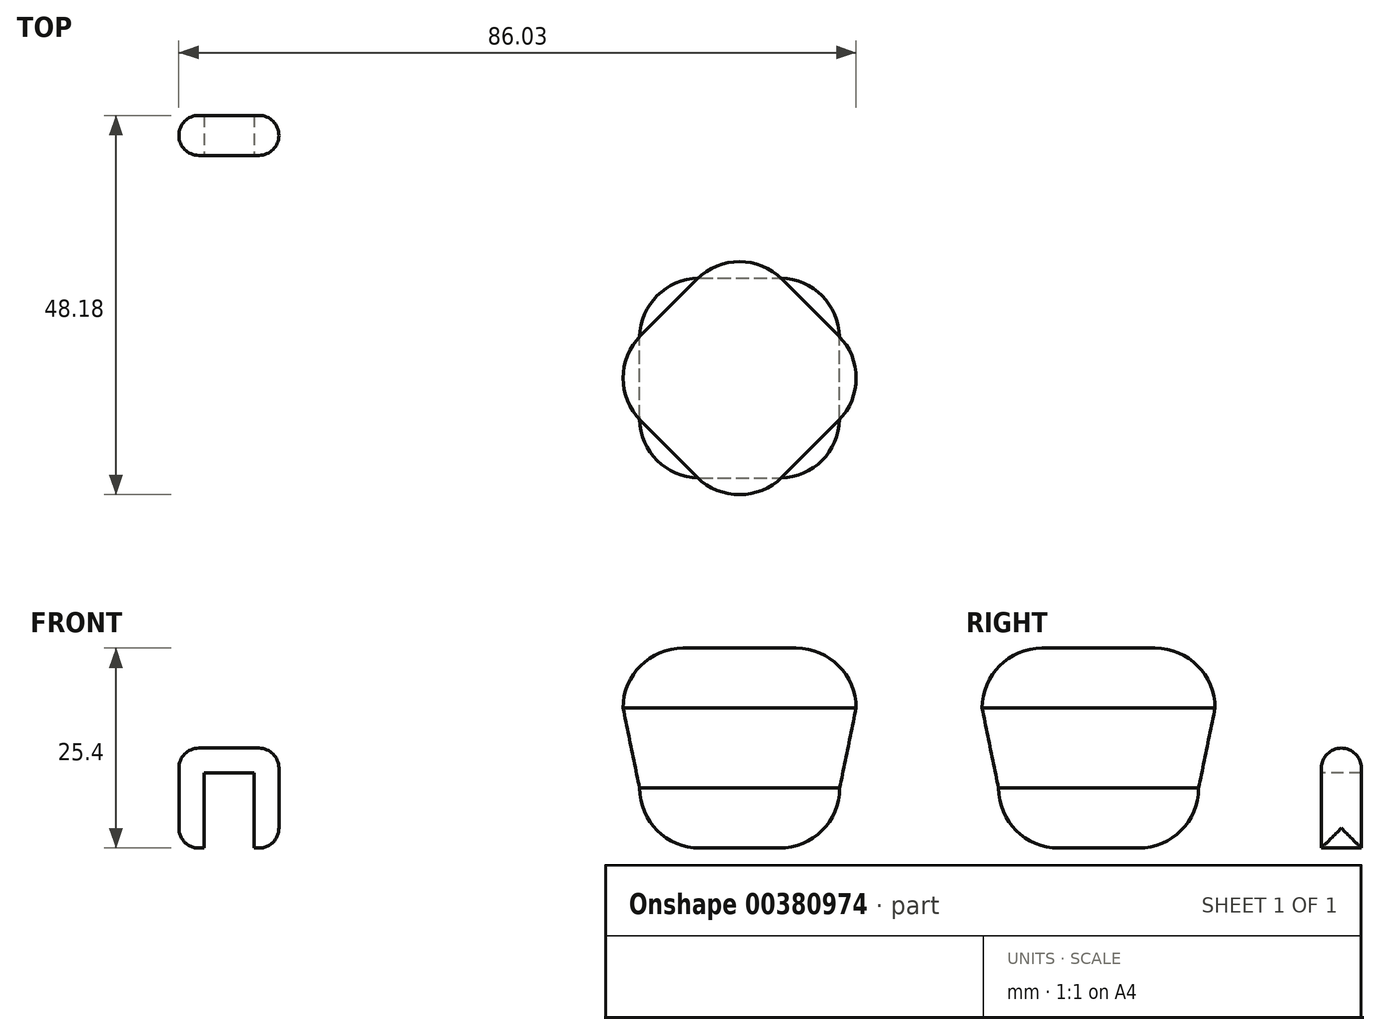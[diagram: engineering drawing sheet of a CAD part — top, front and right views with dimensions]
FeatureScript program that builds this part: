
annotation { "Feature Type Name" : "Feature", "Feature Type Description" : "" }
export const myFeature = defineFeature(function(context is Context, id is Id, definition is map)
    precondition{}
    {
        {
            var Q0;
            Q0=qCreatedBy(makeId("Top.planeOp"),FACE);
            var sketch = newSketch(context, id + "F0", { "sketchPlane" : qUnion([Q0])});
            skLineSegment(sketch, "E0.bottom", {"start": v(0, 0) * mm, "end": v(25.4, 0) * mm});
            skLineSegment(sketch, "E0.top", {"start": v(0, 25.4) * mm, "end": v(25.4, 25.4) * mm});
            skLineSegment(sketch, "E0.left", {"start": v(0, 0) * mm, "end": v(0, 25.4) * mm});
            skLineSegment(sketch, "E0.right", {"start": v(25.4, 0) * mm, "end": v(25.4, 25.4) * mm});
            skSolve(sketch);
        }
        {
            var Q0;
            Q0=makeQuery(id+"F0.imprint","IMPRINT",FACE,{"disambiguationData":[TD([[makeQuery(id+"F0.imprint","IMPRINT",EDGE,{"derivedFrom":sQuery(id+"F0.wireOp",EDGE,"E0.bottom")}),1.0]])]});
            extrude(context, id + "F1", {"entities" : qUnion([Q0]), "depth" : 7.62 * mm});
        }
        {
            var Q0;
            Q0=makeQuery(id+"F1.opExtrude","CAP_FACE",FACE,{"disambiguationData":[OSD([sQuery(id+"F0.wireOp",EDGE,"E0.bottom"),sQuery(id+"F0.wireOp",EDGE,"E0.top"),sQuery(id+"F0.wireOp",EDGE,"E0.left"),sQuery(id+"F0.wireOp",EDGE,"E0.right")])],"isStart":true});
            fillet(context, id + "F2", {"entities" : qUnion([Q0]), "radius" : 7.62 * mm, "tangentPropagation" : true, "allowEdgeOverflow" : false});
        }
        {
            var Q0;
            Q0=makeQuery(id+"F2.opFillet","BLEND_EDGE",EDGE,{"blendedFrom":[makeQuery(id+"F1.opExtrude","CAP_EDGE",EDGE,{"disambiguationData":[OSD([sQuery(id+"F0.wireOp",EDGE,"E0.bottom")])],"isStart":true}),makeQuery(id+"F1.opExtrude","CAP_EDGE",EDGE,{"disambiguationData":[OSD([sQuery(id+"F0.wireOp",EDGE,"E0.right")])],"isStart":true})],"blendedInto":[]});
            var Q1;
            Q1=makeQuery(id+"F2.opFillet","BLEND_EDGE",EDGE,{"blendedFrom":[makeQuery(id+"F1.opExtrude","CAP_EDGE",EDGE,{"disambiguationData":[OSD([sQuery(id+"F0.wireOp",EDGE,"E0.bottom")])],"isStart":true}),makeQuery(id+"F1.opExtrude","CAP_EDGE",EDGE,{"disambiguationData":[OSD([sQuery(id+"F0.wireOp",EDGE,"E0.left")])],"isStart":true})],"blendedInto":[]});
            var Q2;
            Q2=makeQuery(id+"F2.opFillet","BLEND_EDGE",EDGE,{"blendedFrom":[makeQuery(id+"F1.opExtrude","CAP_EDGE",EDGE,{"disambiguationData":[OSD([sQuery(id+"F0.wireOp",EDGE,"E0.top")])],"isStart":true}),makeQuery(id+"F1.opExtrude","CAP_EDGE",EDGE,{"disambiguationData":[OSD([sQuery(id+"F0.wireOp",EDGE,"E0.left")])],"isStart":true})],"blendedInto":[]});
            var Q3;
            Q3=makeQuery(id+"F2.opFillet","BLEND_EDGE",EDGE,{"blendedFrom":[makeQuery(id+"F1.opExtrude","CAP_EDGE",EDGE,{"disambiguationData":[OSD([sQuery(id+"F0.wireOp",EDGE,"E0.top")])],"isStart":true}),makeQuery(id+"F1.opExtrude","CAP_EDGE",EDGE,{"disambiguationData":[OSD([sQuery(id+"F0.wireOp",EDGE,"E0.right")])],"isStart":true})],"blendedInto":[]});
            fillet(context, id + "F3", {"entities" : qUnion([Q0, Q1, Q2, Q3]), "radius" : 7.62 * mm, "tangentPropagation" : true, "allowEdgeOverflow" : false});
        }
        {
            var Q0;
            Q0=makeQuery(id+"F1.opExtrude","CAP_FACE",FACE,{"disambiguationData":[OSD([sQuery(id+"F0.wireOp",EDGE,"E0.bottom"),sQuery(id+"F0.wireOp",EDGE,"E0.top"),sQuery(id+"F0.wireOp",EDGE,"E0.left"),sQuery(id+"F0.wireOp",EDGE,"E0.right")])],"isStart":false});
            cPlane(context, id + "F4", {"entities" : qUnion([Q0]), "cplaneType" : CPlaneType.OFFSET, "offset" : 10.16 * mm, "width" : 152.4 * mm, "height" : 152.4 * mm});
        }
        {
            var Q0;
            Q0=qCreatedBy(id+"F4.planeOp",FACE);
            var sketch = newSketch(context, id + "F5", { "sketchPlane" : qUnion([Q0])});
            skLineSegment(sketch, "E1", {"start": v(0, 0) * mm, "end": v(0, 25.4) * mm});
            skLineSegment(sketch, "E2", {"start": v(0, 25.4) * mm, "end": v(25.4, 25.4) * mm});
            skLineSegment(sketch, "E3", {"start": v(25.4, 25.4) * mm, "end": v(25.4, 0) * mm});
            skLineSegment(sketch, "E4", {"start": v(25.4, 0) * mm, "end": v(0, 0) * mm});
            skSolve(sketch);
        }
        {
            var Q0;
            Q0=makeQuery(id+"F5.imprint","IMPRINT",FACE,{"disambiguationData":[TD([[makeQuery(id+"F5.imprint","IMPRINT",EDGE,{"derivedFrom":sQuery(id+"F5.wireOp",EDGE,"E1")}),-1.0]])]});
            extrude(context, id + "F6", {"entities" : qUnion([Q0]), "depth" : 7.62 * mm});
        }
        {
            var Q0;
            Q0=makeQuery(id+"F6.opExtrude","CAP_FACE",FACE,{"disambiguationData":[OSD([sQuery(id+"F5.wireOp",EDGE,"E1"),sQuery(id+"F5.wireOp",EDGE,"E2"),sQuery(id+"F5.wireOp",EDGE,"E3"),sQuery(id+"F5.wireOp",EDGE,"E4")])],"isStart":false});
            fillet(context, id + "F7", {"entities" : qUnion([Q0]), "radius" : 7.62 * mm, "tangentPropagation" : true, "allowEdgeOverflow" : false});
        }
        {
            var Q0;
            Q0=makeQuery(id+"F7.opFillet","BLEND_EDGE",EDGE,{"blendedFrom":[makeQuery(id+"F6.opExtrude","CAP_EDGE",EDGE,{"disambiguationData":[OSD([sQuery(id+"F5.wireOp",EDGE,"E3")])],"isStart":false}),makeQuery(id+"F6.opExtrude","CAP_EDGE",EDGE,{"disambiguationData":[OSD([sQuery(id+"F5.wireOp",EDGE,"E4")])],"isStart":false})],"blendedInto":[]});
            var Q1;
            Q1=makeQuery(id+"F7.opFillet","BLEND_EDGE",EDGE,{"blendedFrom":[makeQuery(id+"F6.opExtrude","CAP_EDGE",EDGE,{"disambiguationData":[OSD([sQuery(id+"F5.wireOp",EDGE,"E1")])],"isStart":false}),makeQuery(id+"F6.opExtrude","CAP_EDGE",EDGE,{"disambiguationData":[OSD([sQuery(id+"F5.wireOp",EDGE,"E4")])],"isStart":false})],"blendedInto":[]});
            var Q2;
            Q2=makeQuery(id+"F7.opFillet","BLEND_EDGE",EDGE,{"blendedFrom":[makeQuery(id+"F6.opExtrude","CAP_EDGE",EDGE,{"disambiguationData":[OSD([sQuery(id+"F5.wireOp",EDGE,"E1")])],"isStart":false}),makeQuery(id+"F6.opExtrude","CAP_EDGE",EDGE,{"disambiguationData":[OSD([sQuery(id+"F5.wireOp",EDGE,"E2")])],"isStart":false})],"blendedInto":[]});
            var Q3;
            Q3=makeQuery(id+"F7.opFillet","BLEND_EDGE",EDGE,{"blendedFrom":[makeQuery(id+"F6.opExtrude","CAP_EDGE",EDGE,{"disambiguationData":[OSD([sQuery(id+"F5.wireOp",EDGE,"E2")])],"isStart":false}),makeQuery(id+"F6.opExtrude","CAP_EDGE",EDGE,{"disambiguationData":[OSD([sQuery(id+"F5.wireOp",EDGE,"E3")])],"isStart":false})],"blendedInto":[]});
            fillet(context, id + "F8", {"entities" : qUnion([Q0, Q1, Q2, Q3]), "radius" : 7.62 * mm, "tangentPropagation" : true, "allowEdgeOverflow" : false});
        }
        {
            var Q0;
            Q0=qCreatedBy(makeId("Front.planeOp"),FACE);
            cPlane(context, id + "F9", {"entities" : qUnion([Q0]), "cplaneType" : CPlaneType.OFFSET, "offset" : 12.7 * mm, "oppositeDirection" : true, "width" : 152.4 * mm, "height" : 152.4 * mm});
        }
        {
            var Q0;
            Q0=qCreatedBy(id+"F9.planeOp",FACE);
            var sketch = newSketch(context, id + "F10", { "sketchPlane" : qUnion([Q0])});
            skLineSegment(sketch, "E5.0", {"start": v(17.78, 25.4) * mm, "end": v(7.62, 25.4) * mm});
            skLineSegment(sketch, "E6", {"start": v(12.7, 25.4) * mm, "end": v(12.7, 70.24) * mm, "construction": true});
            skSolve(sketch);
        }
        {
            var Q0;
            Q0=makeQuery(id+"F6.opExtrude","SWEPT_BODY",BODY,{"disambiguationData":[OSD([sQuery(id+"F5.wireOp",EDGE,"E1"),sQuery(id+"F5.wireOp",EDGE,"E2"),sQuery(id+"F5.wireOp",EDGE,"E3"),sQuery(id+"F5.wireOp",EDGE,"E4")])]});
            var Q1;
            Q1=sQuery(id+"F10.wireOp",EDGE,"E6");
            transform(context, id + "F11", {"entities" : qUnion([Q0]), "transformType" : TransformType.ROTATION, "transformAxis" : qUnion([Q1]), "angle" : 45 * degree, "makeCopy" : false});
        }
        {
            var Q0;
            Q0=makeQuery(id+"F1.opExtrude","CAP_FACE",FACE,{"disambiguationData":[OSD([sQuery(id+"F0.wireOp",EDGE,"E0.bottom"),sQuery(id+"F0.wireOp",EDGE,"E0.top"),sQuery(id+"F0.wireOp",EDGE,"E0.left"),sQuery(id+"F0.wireOp",EDGE,"E0.right")])],"isStart":false});
            var Q1;
            Q1=makeQuery(id+"F6.opExtrude","CAP_FACE",FACE,{"disambiguationData":[OSD([sQuery(id+"F5.wireOp",EDGE,"E1"),sQuery(id+"F5.wireOp",EDGE,"E2"),sQuery(id+"F5.wireOp",EDGE,"E3"),sQuery(id+"F5.wireOp",EDGE,"E4")])],"isStart":true});
            loft(context, id + "F12", {"sheetProfilesArray" : [{ "sheetProfileEntities" : qUnion([Q0]) }, { "sheetProfileEntities" : qUnion([Q1]) }]});
        }
        {
            var Q0;
            Q0=qCreatedBy(makeId("Top.planeOp"),FACE);
            var sketch = newSketch(context, id + "F13", { "sketchPlane" : qUnion([Q0])});
            skLineSegment(sketch, "E7.bottom", {"start": v(-58.53, 46.08) * mm, "end": v(-45.83, 46.08) * mm});
            skLineSegment(sketch, "E7.top", {"start": v(-58.53, 41) * mm, "end": v(-45.83, 41) * mm});
            skLineSegment(sketch, "E7.left", {"start": v(-58.53, 46.08) * mm, "end": v(-58.53, 41) * mm});
            skLineSegment(sketch, "E7.right", {"start": v(-45.83, 46.08) * mm, "end": v(-45.83, 41) * mm});
            skSolve(sketch);
        }
        {
            var Q0;
            Q0=makeQuery(id+"F13.imprint","IMPRINT",FACE,{"disambiguationData":[TD([[makeQuery(id+"F13.imprint","IMPRINT",EDGE,{"derivedFrom":sQuery(id+"F13.wireOp",EDGE,"E7.bottom")}),-1.0]])]});
            extrude(context, id + "F14", {"entities" : qUnion([Q0]), "depth" : 12.7 * mm});
        }
        {
            var Q0;
            Q0=makeQuery(id+"F14.opExtrude","SWEPT_FACE",FACE,{"disambiguationData":[OSD([sQuery(id+"F13.wireOp",EDGE,"E7.top")])]});
            var sketch = newSketch(context, id + "F15", { "sketchPlane" : qUnion([Q0])});
            skLineSegment(sketch, "E8", {"start": v(-52.18, 0) * mm, "end": v(-58.53, 0) * mm});
            skLineSegment(sketch, "E9", {"start": v(-58.53, 0) * mm, "end": v(-55.15, 0) * mm});
            skLineSegment(sketch, "E10", {"start": v(-55.35, 0) * mm, "end": v(-55.35, 9.53) * mm});
            skLineSegment(sketch, "E11", {"start": v(-55.35, 12.7) * mm, "end": v(-52.18, 12.7) * mm});
            skLineSegment(sketch, "E12", {"start": v(-52.18, 12.7) * mm, "end": v(-45.83, 12.7) * mm});
            skLineSegment(sketch, "E13", {"start": v(-45.83, 12.7) * mm, "end": v(-49, 12.7) * mm});
            skLineSegment(sketch, "E14", {"start": v(-49, 9.53) * mm, "end": v(-49, 0) * mm});
            skLineSegment(sketch, "E15", {"start": v(-49, 0) * mm, "end": v(-45.83, 0) * mm});
            skLineSegment(sketch, "E16", {"start": v(-45.83, 0) * mm, "end": v(-45.83, 12.7) * mm});
            skLineSegment(sketch, "E17", {"start": v(-45.83, 6.35) * mm, "end": v(-45.83, 12.7) * mm});
            skLineSegment(sketch, "E18", {"start": v(-49, 9.53) * mm, "end": v(-55.35, 9.53) * mm});
            skPoint(sketch, "E19.orphan", {"position": v(-45.83, 9.53) * mm});
            skSolve(sketch);
        }
        {
            var Q0;
            {var subQ3=sQuery(id+"F15.wireOp",EDGE,"E8");Q0=makeQuery(id+"F15.imprint","IMPRINT",FACE,{"disambiguationData":[TD([[makeQuery(id+"F15.imprint","IMPRINT",EDGE,{"derivedFrom":subQ3}),1.0]])]});}
            extrude(context, id + "F16", {"entities" : qUnion([Q0]), "operationType" : NewBodyOperationType.REMOVE, "oppositeDirection" : true, "depth" : 5.08 * mm});
        }
        {
            var Q0;
            Q0=makeQuery(id+"F14.opExtrude","CAP_FACE",FACE,{"disambiguationData":[OSD([sQuery(id+"F13.wireOp",EDGE,"E7.bottom"),sQuery(id+"F13.wireOp",EDGE,"E7.top"),sQuery(id+"F13.wireOp",EDGE,"E7.left"),sQuery(id+"F13.wireOp",EDGE,"E7.right")])],"isStart":false});
            var Q1;
            Q1=makeQuery(id+"F14.opExtrude","SWEPT_FACE",FACE,{"disambiguationData":[OSD([sQuery(id+"F13.wireOp",EDGE,"E7.right")])]});
            var Q2;
            Q2=makeQuery(id+"F14.opExtrude","SWEPT_FACE",FACE,{"disambiguationData":[OSD([sQuery(id+"F13.wireOp",EDGE,"E7.left")])]});
            fillet(context, id + "F17", {"entities" : qUnion([Q0, Q1, Q2]), "radius" : 2.54 * mm, "tangentPropagation" : true, "allowEdgeOverflow" : false});
        }
    });
